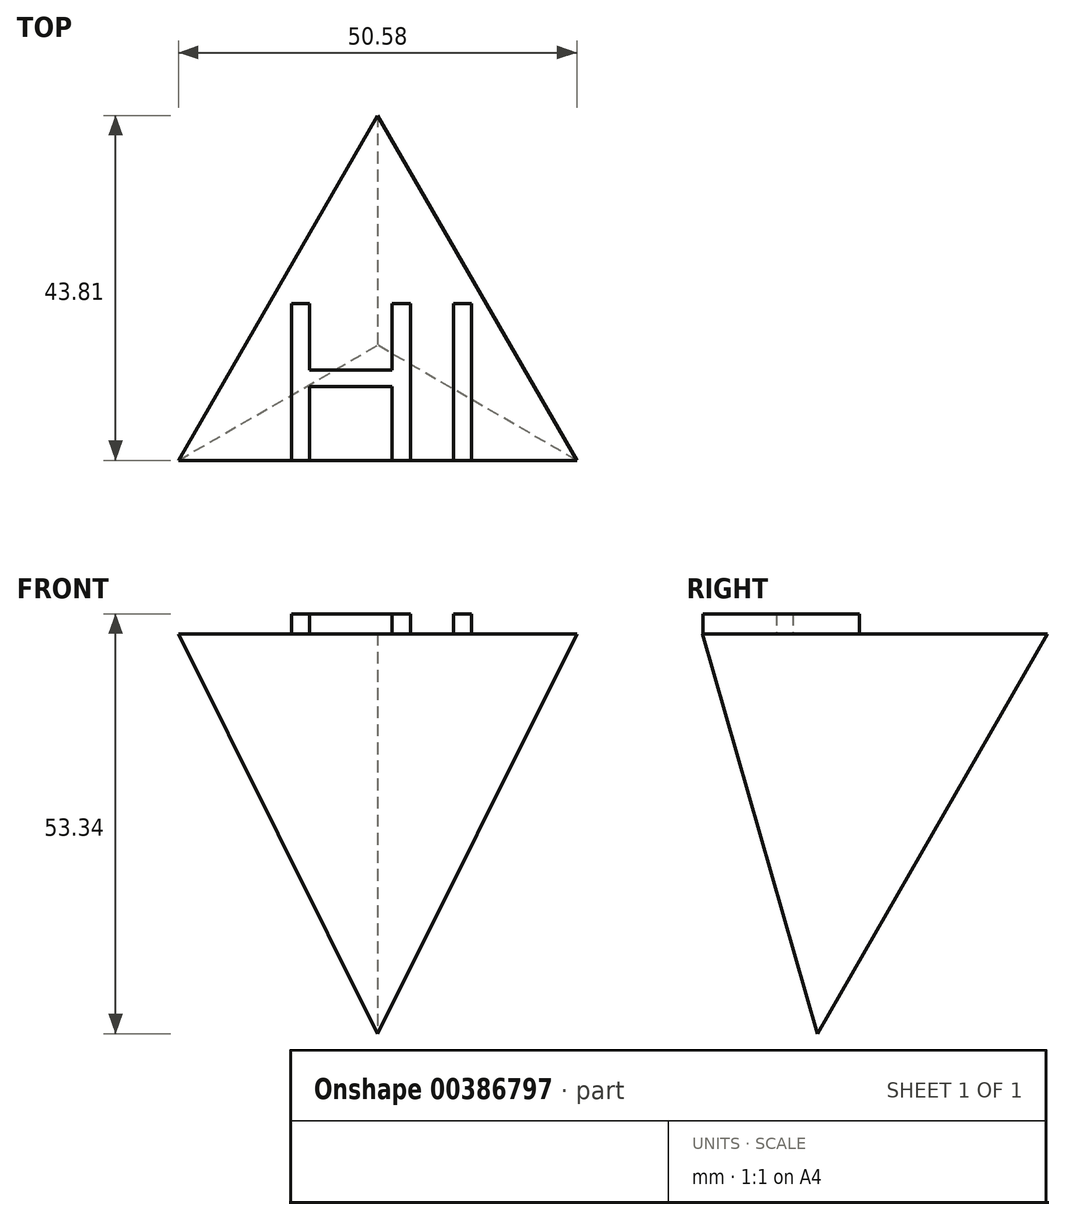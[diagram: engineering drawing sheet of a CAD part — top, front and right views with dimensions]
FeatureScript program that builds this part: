
annotation { "Feature Type Name" : "Feature", "Feature Type Description" : "" }
export const myFeature = defineFeature(function(context is Context, id is Id, definition is map)
    precondition{}
    {
        {
            var Q0;
            Q0=qCreatedBy(makeId("Top.planeOp"),FACE);
            var sketch = newSketch(context, id + "F0", { "sketchPlane" : qUnion([Q0])});
            skPoint(sketch, "E0", {"position": v(0, 0) * mm});
            skSolve(sketch);
        }
        {
            var Q0;
            Q0=qCreatedBy(makeId("Top.planeOp"),FACE);
            cPlane(context, id + "F1", {"entities" : qUnion([Q0]), "cplaneType" : CPlaneType.OFFSET, "offset" : 50.8 * mm, "width" : 152.4 * mm, "height" : 152.4 * mm});
        }
        {
            var Q0;
            Q0=qCreatedBy(id+"F1.planeOp",FACE);
            var sketch = newSketch(context, id + "F2", { "sketchPlane" : qUnion([Q0])});
            skCircle(sketch, "E1.cCircle", {"center": v(0, 0) * mm, "radius": 14.6 * mm, "construction": true});
            skLineSegment(sketch, "E1.0", {"start": v(25.3, -14.6) * mm, "end": v(-25.3, -14.6) * mm});
            skLineSegment(sketch, "E1.1", {"start": v(-25.3, -14.6) * mm, "end": v(0, 29.2) * mm});
            skLineSegment(sketch, "E1.2", {"start": v(0, 29.2) * mm, "end": v(25.3, -14.6) * mm});
            skPoint(sketch, "E1.0.midPoint", {"position": v(0, -14.6) * mm});
            skSolve(sketch);
        }
        {
            var Q0;
            Q0=makeQuery(id+"F2.imprint","IMPRINT",FACE,{"disambiguationData":[TD([[makeQuery(id+"F2.imprint","IMPRINT",EDGE,{"derivedFrom":sQuery(id+"F2.wireOp",EDGE,"E1.0")}),-1.0]])]});
            var Q1;
            Q1=sQuery(id+"F0.wireOp",VERTEX,"E0");
            loft(context, id + "F3", {"sheetProfilesArray" : [{ "sheetProfileEntities" : qUnion([Q0]) }, { "sheetProfileEntities" : qUnion([Q1]) }]});
        }
        {
            var Q0;
            Q0=makeQuery(id+"F3.opLoft","CAP_FACE",FACE,{"disambiguationData":[OSD([makeQuery(id+"F2.imprint","IMPRINT",FACE,{"disambiguationData":[TD([[makeQuery(id+"F2.imprint","IMPRINT",EDGE,{"derivedFrom":sQuery(id+"F2.wireOp",EDGE,"E1.0")}),-1.0]])]})])],"isStart":true});
            var sketch = newSketch(context, id + "F4", { "sketchPlane" : qUnion([Q0])});
            skText(sketch, "E2", { "text": "HI\n", "fontName": "OpenSans-Regular.ttf"});
            const initialGuessF4  = {"E2": [-0.0137, -0.0146, 1, 0, 0.02007]};
            skSetInitialGuess(sketch, initialGuessF4);
            skSolve(sketch);
        }
        {
            var Q0;
            Q0 = qSketchRegion(id + "F4", true);
            extrude(context, id + "F5", {"entities" : qUnion([Q0]), "operationType" : NewBodyOperationType.ADD, "depth" : 2.54 * mm});
        }
    });
